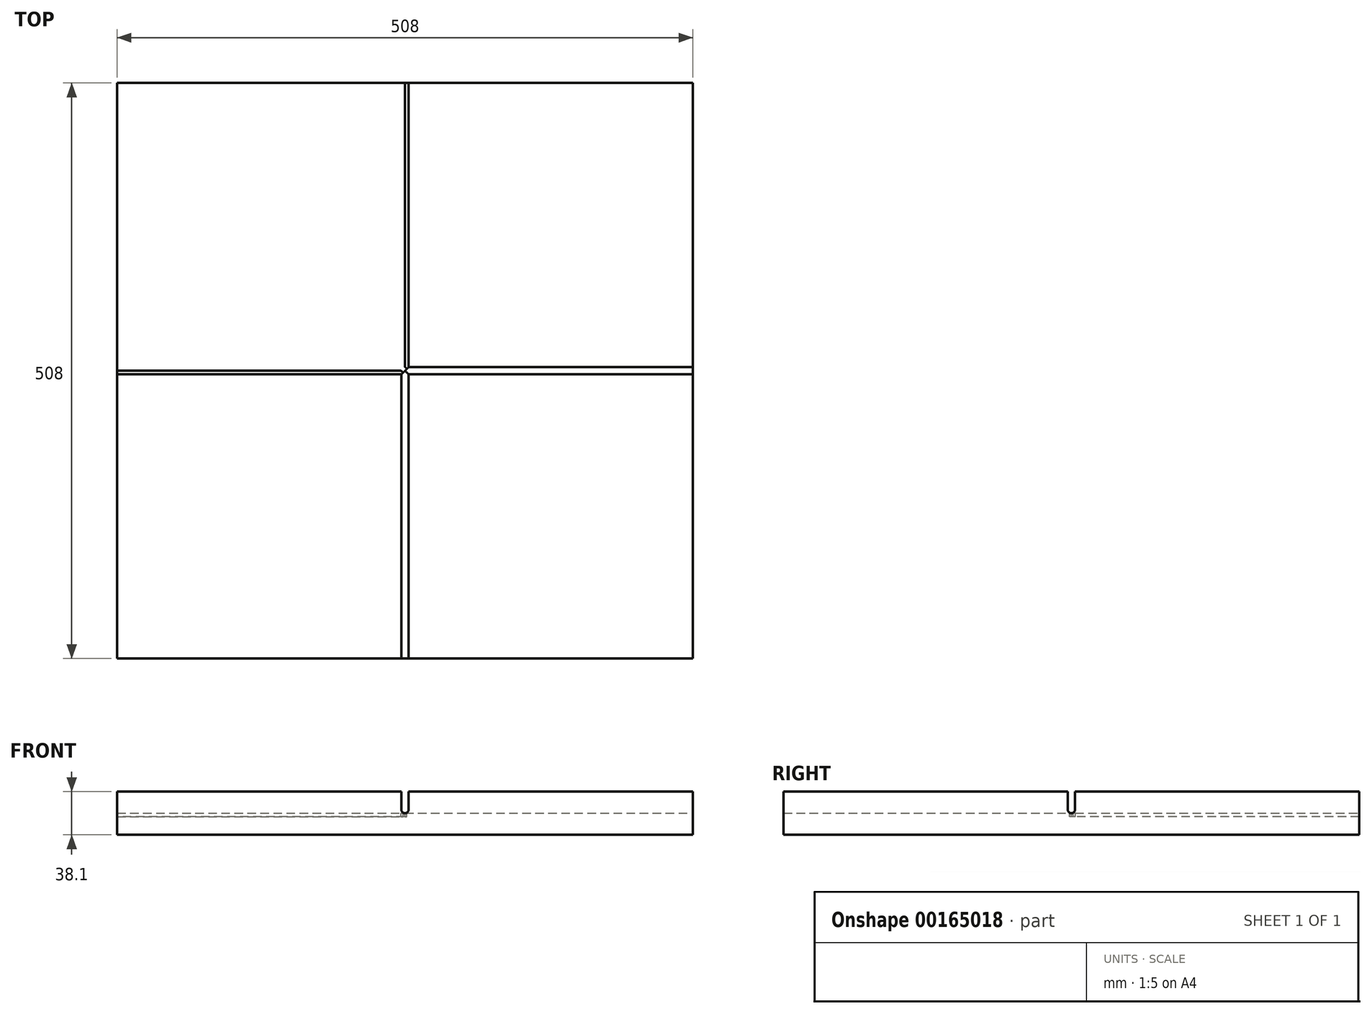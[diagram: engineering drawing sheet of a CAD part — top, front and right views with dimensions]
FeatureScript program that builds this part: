
annotation { "Feature Type Name" : "Feature", "Feature Type Description" : "" }
export const myFeature = defineFeature(function(context is Context, id is Id, definition is map)
    precondition{}
    {
        {
            var Q0;
            Q0=qCreatedBy(makeId("Top.planeOp"),FACE);
            var sketch = newSketch(context, id + "F0", { "sketchPlane" : qUnion([Q0])});
            skLineSegment(sketch, "E0.bottom", {"start": v(254, 254) * mm, "end": v(-254, 254) * mm});
            skLineSegment(sketch, "E0.top", {"start": v(254, -254) * mm, "end": v(-254, -254) * mm});
            skLineSegment(sketch, "E0.left", {"start": v(254, 254) * mm, "end": v(254, -254) * mm});
            skLineSegment(sketch, "E0.right", {"start": v(-254, 254) * mm, "end": v(-254, -254) * mm});
            skPoint(sketch, "E0.middle", {"position": v(0, 0) * mm});
            skSolve(sketch);
        }
        {
            var Q0;
            Q0 = qSketchRegion(id + "F0", true);
            extrude(context, id + "F1", {"entities" : qUnion([Q0]), "depth" : 38.1 * mm});
        }
        {
            var Q0;
            Q0=makeQuery(id+"F1.opExtrude","CAP_FACE",FACE,{"disambiguationData":[OSD([sQuery(id+"F0.wireOp",EDGE,"E0.bottom"),sQuery(id+"F0.wireOp",EDGE,"E0.top"),sQuery(id+"F0.wireOp",EDGE,"E0.left"),sQuery(id+"F0.wireOp",EDGE,"E0.right")])],"isStart":false});
            var sketch = newSketch(context, id + "F2", { "sketchPlane" : qUnion([Q0])});
            skLineSegment(sketch, "E1.bottom", {"start": v(254, -3.17) * mm, "end": v(-254, -3.17) * mm});
            skLineSegment(sketch, "E1.top", {"start": v(254, 3.18) * mm, "end": v(-254, 3.18) * mm});
            skLineSegment(sketch, "E1.left", {"start": v(254, -3.17) * mm, "end": v(254, 3.18) * mm});
            skLineSegment(sketch, "E1.right", {"start": v(-254, -3.17) * mm, "end": v(-254, 3.18) * mm});
            skPoint(sketch, "E1.middle", {"position": v(0, 0) * mm});
            skLineSegment(sketch, "E2.bottom", {"start": v(3.18, -254) * mm, "end": v(-3.18, -254) * mm});
            skLineSegment(sketch, "E2.top", {"start": v(3.18, 254) * mm, "end": v(-3.18, 254) * mm});
            skLineSegment(sketch, "E2.left", {"start": v(3.18, -254) * mm, "end": v(3.18, 254) * mm});
            skLineSegment(sketch, "E2.right", {"start": v(-3.18, -254) * mm, "end": v(-3.18, 254) * mm});
            skSolve(sketch);
        }
        {
            var Q0;
            Q0 = qSketchRegion(id + "F2", true);
            extrude(context, id + "F3", {"entities" : qUnion([Q0]), "operationType" : NewBodyOperationType.REMOVE, "oppositeDirection" : true, "depth" : 19.05 * mm});
        }
        {
            var Q0;
            {var subQ0=sQuery(id+"F2.wireOp",EDGE,"E1.bottom");Q0=makeQuery(id+"F3.boolean.opBoolean","COPY",EDGE,{"derivedFrom":makeQuery(id+"F3.opExtrude","CAP_EDGE",EDGE,{"disambiguationData":[OSD([subQ0]),TDD([makeQuery(id+"F2.imprint","IMPRINT",EDGE,{"disambiguationData":[TD([[makeQuery(id+"F2.imprint","INTERSECT",VERTEX,{"derivedFrom":[subQ0,sQuery(id+"F2.wireOp",EDGE,"E2.right")]}),-1.0]])],"derivedFrom":subQ0})])],"isStart":false})});}
            var Q1;
            {var subQ0=sQuery(id+"F2.wireOp",EDGE,"E2.right");Q1=makeQuery(id+"F3.boolean.opBoolean","COPY",EDGE,{"derivedFrom":makeQuery(id+"F3.opExtrude","CAP_EDGE",EDGE,{"disambiguationData":[OSD([subQ0]),TDD([makeQuery(id+"F2.imprint","IMPRINT",EDGE,{"disambiguationData":[TD([[makeQuery(id+"F2.imprint","INTERSECT",VERTEX,{"derivedFrom":[sQuery(id+"F2.wireOp",EDGE,"E1.bottom"),subQ0]}),1.0]])],"derivedFrom":subQ0})])],"isStart":false})});}
            var Q2;
            {var subQ0=sQuery(id+"F2.wireOp",EDGE,"E2.left");Q2=makeQuery(id+"F3.boolean.opBoolean","COPY",EDGE,{"derivedFrom":makeQuery(id+"F3.opExtrude","CAP_EDGE",EDGE,{"disambiguationData":[OSD([subQ0]),TDD([makeQuery(id+"F2.imprint","IMPRINT",EDGE,{"disambiguationData":[TD([[makeQuery(id+"F2.imprint","INTERSECT",VERTEX,{"derivedFrom":[sQuery(id+"F2.wireOp",EDGE,"E1.bottom"),subQ0]}),1.0]])],"derivedFrom":subQ0})])],"isStart":false})});}
            var Q3;
            {var subQ0=sQuery(id+"F2.wireOp",EDGE,"E1.bottom");Q3=makeQuery(id+"F3.boolean.opBoolean","COPY",EDGE,{"derivedFrom":makeQuery(id+"F3.opExtrude","CAP_EDGE",EDGE,{"disambiguationData":[OSD([subQ0]),TDD([makeQuery(id+"F2.imprint","IMPRINT",EDGE,{"disambiguationData":[TD([[makeQuery(id+"F2.imprint","INTERSECT",VERTEX,{"derivedFrom":[subQ0,sQuery(id+"F2.wireOp",EDGE,"E2.left")]}),1.0]])],"derivedFrom":subQ0})])],"isStart":false})});}
            var Q4;
            {var subQ0=sQuery(id+"F2.wireOp",EDGE,"E1.top");Q4=makeQuery(id+"F3.boolean.opBoolean","COPY",EDGE,{"derivedFrom":makeQuery(id+"F3.opExtrude","CAP_EDGE",EDGE,{"disambiguationData":[OSD([subQ0]),TDD([makeQuery(id+"F2.imprint","IMPRINT",EDGE,{"disambiguationData":[TD([[makeQuery(id+"F2.imprint","INTERSECT",VERTEX,{"derivedFrom":[subQ0,sQuery(id+"F2.wireOp",EDGE,"E2.left")]}),1.0]])],"derivedFrom":subQ0})])],"isStart":false})});}
            var Q5;
            {var subQ0=sQuery(id+"F2.wireOp",EDGE,"E2.left");Q5=makeQuery(id+"F3.boolean.opBoolean","COPY",EDGE,{"derivedFrom":makeQuery(id+"F3.opExtrude","CAP_EDGE",EDGE,{"disambiguationData":[OSD([subQ0]),TDD([makeQuery(id+"F2.imprint","IMPRINT",EDGE,{"disambiguationData":[TD([[makeQuery(id+"F2.imprint","INTERSECT",VERTEX,{"derivedFrom":[sQuery(id+"F2.wireOp",EDGE,"E1.top"),subQ0]}),-1.0]])],"derivedFrom":subQ0})])],"isStart":false})});}
            var Q6;
            {var subQ0=sQuery(id+"F2.wireOp",EDGE,"E2.right");Q6=makeQuery(id+"F3.boolean.opBoolean","COPY",EDGE,{"derivedFrom":makeQuery(id+"F3.opExtrude","CAP_EDGE",EDGE,{"disambiguationData":[OSD([subQ0]),TDD([makeQuery(id+"F2.imprint","IMPRINT",EDGE,{"disambiguationData":[TD([[makeQuery(id+"F2.imprint","INTERSECT",VERTEX,{"derivedFrom":[sQuery(id+"F2.wireOp",EDGE,"E1.top"),subQ0]}),-1.0]])],"derivedFrom":subQ0})])],"isStart":false})});}
            var Q7;
            {var subQ0=sQuery(id+"F2.wireOp",EDGE,"E1.top");Q7=makeQuery(id+"F3.boolean.opBoolean","COPY",EDGE,{"derivedFrom":makeQuery(id+"F3.opExtrude","CAP_EDGE",EDGE,{"disambiguationData":[OSD([subQ0]),TDD([makeQuery(id+"F2.imprint","IMPRINT",EDGE,{"disambiguationData":[TD([[makeQuery(id+"F2.imprint","INTERSECT",VERTEX,{"derivedFrom":[subQ0,sQuery(id+"F2.wireOp",EDGE,"E2.right")]}),-1.0]])],"derivedFrom":subQ0})])],"isStart":false})});}
            fillet(context, id + "F4", {"entities" : qUnion([Q0, Q1, Q2, Q3, Q4, Q5, Q6, Q7]), "radius" : 3.17 * mm, "tangentPropagation" : true, "allowEdgeOverflow" : false});
        }
        {
            var Q0;
            {var subQ0=sQuery(id+"F0.wireOp",EDGE,"E0.bottom");var subQ1=sQuery(id+"F0.wireOp",EDGE,"E0.right");var subQ2=sQuery(id+"F2.wireOp",EDGE,"E1.top");var subQ3=sQuery(id+"F2.wireOp",EDGE,"E2.right");var subQ4=makeQuery(id+"F2.imprint","INTERSECT",VERTEX,{"derivedFrom":[subQ2,subQ3]});Q0=makeQuery(id+"F3.boolean.opBoolean","SPLIT",FACE,{"disambiguationData":[TD([makeQuery(id+"F3.opExtrude","SWEPT_FACE",FACE,{"disambiguationData":[OSD([subQ2]),TDD([makeQuery(id+"F2.imprint","IMPRINT",EDGE,{"disambiguationData":[TD([[subQ4,-1.0]])],"derivedFrom":subQ2})])]})])],"derivedFrom":makeQuery(id+"F1.opExtrude","CAP_FACE",FACE,{"disambiguationData":[OSD([subQ0,sQuery(id+"F0.wireOp",EDGE,"E0.top"),sQuery(id+"F0.wireOp",EDGE,"E0.left"),subQ1])],"isStart":false})});}
            var sketch = newSketch(context, id + "F5", { "sketchPlane" : qUnion([Q0])});
            skLineSegment(sketch, "E3.bottom", {"start": v(-254, 254) * mm, "end": v(0, 254) * mm});
            skLineSegment(sketch, "E3.top", {"start": v(-254, 0) * mm, "end": v(-3.37, 0) * mm});
            skLineSegment(sketch, "E3.left", {"start": v(-254, 254) * mm, "end": v(-254, 0) * mm});
            skLineSegment(sketch, "E3.right", {"start": v(0, 254) * mm, "end": v(0, 3.37) * mm});
            skLineSegment(sketch, "E4.bottom", {"start": v(0, 3.37) * mm, "end": v(-3.37, 0) * mm, "construction": true});
            skLineSegment(sketch, "E4.top", {"start": v(1.68, 1.68) * mm, "end": v(-1.68, -1.68) * mm});
            skLineSegment(sketch, "E4.left", {"start": v(0, 3.37) * mm, "end": v(1.68, 1.68) * mm});
            skLineSegment(sketch, "E4.right", {"start": v(-3.37, 0) * mm, "end": v(-1.68, -1.68) * mm});
            skLineSegment(sketch, "E5", {"start": v(0, 254) * mm, "end": v(-254, 0) * mm, "construction": true});
            skLineSegment(sketch, "E6", {"start": v(-254, 254) * mm, "end": v(-127, 127) * mm, "construction": true});
            skLineSegment(sketch, "E7", {"start": v(-127, 127) * mm, "end": v(-1.68, 1.68) * mm, "construction": true});
            skSolve(sketch);
        }
        {
            var Q0;
            Q0 = qSketchRegion(id + "F5", true);
            extrude(context, id + "F6", {"entities" : qUnion([Q0]), "operationType" : NewBodyOperationType.REMOVE, "oppositeDirection" : true, "depth" : 22.22 * mm});
        }
        {
            var Q0;
            Q0=makeQuery(id+"F1.opExtrude","CAP_FACE",FACE,{"disambiguationData":[OSD([sQuery(id+"F0.wireOp",EDGE,"E0.bottom"),sQuery(id+"F0.wireOp",EDGE,"E0.top"),sQuery(id+"F0.wireOp",EDGE,"E0.left"),sQuery(id+"F0.wireOp",EDGE,"E0.right")])],"isStart":true});
            var sketch = newSketch(context, id + "F7", { "sketchPlane" : qUnion([Q0])});
            skCircle(sketch, "E8", {"center": v(0, 0) * mm, "radius": 6.35 * mm});
            skSolve(sketch);
        }
    });
